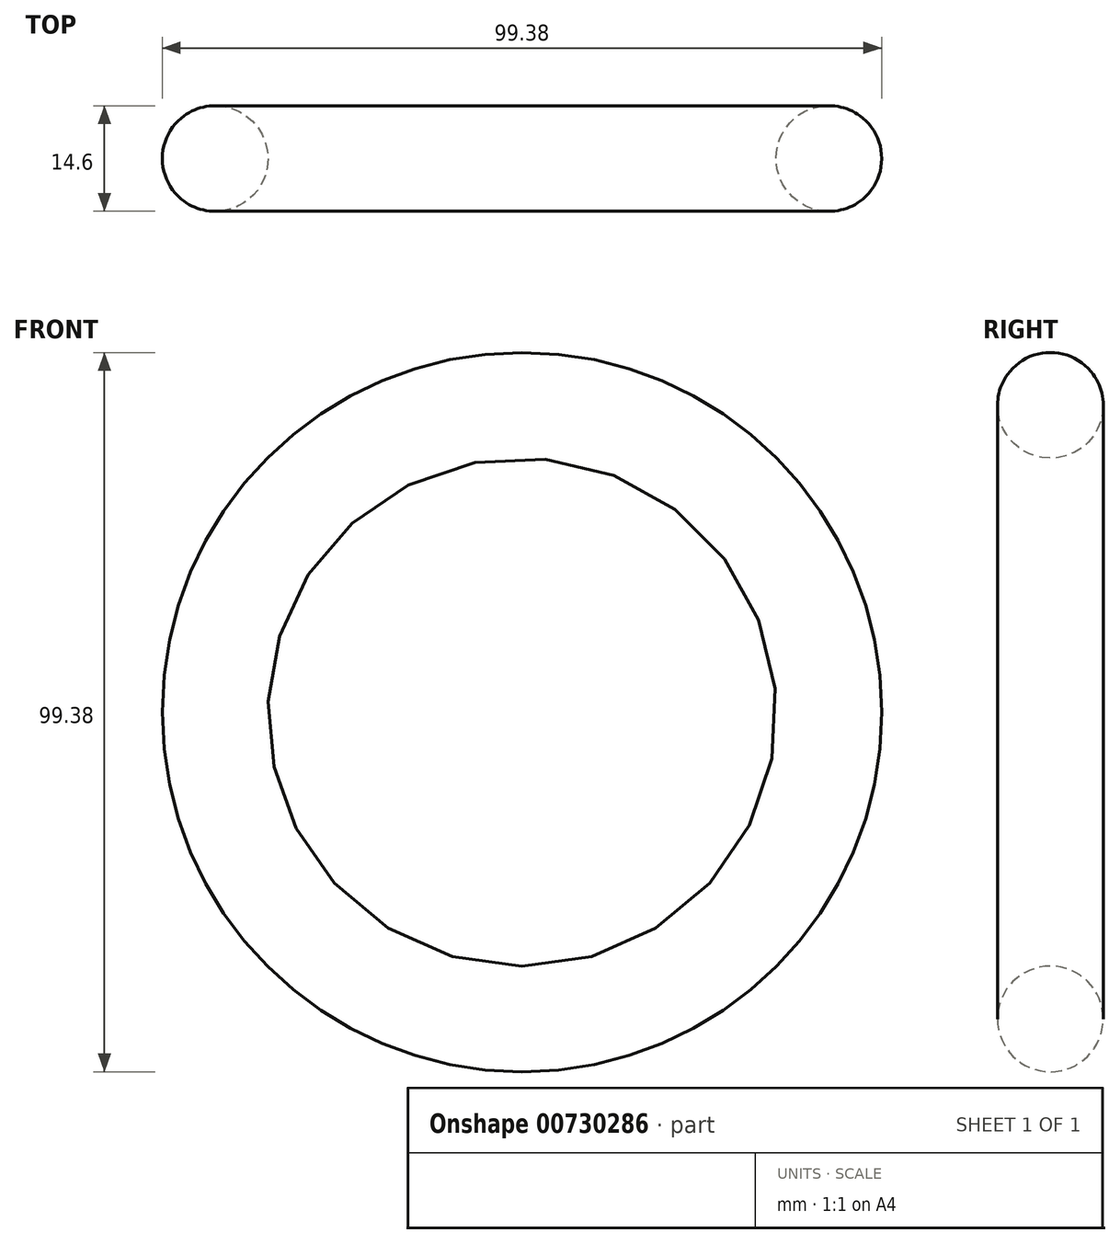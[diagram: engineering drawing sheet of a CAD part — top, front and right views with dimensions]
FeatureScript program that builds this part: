
annotation { "Feature Type Name" : "Feature", "Feature Type Description" : "" }
export const myFeature = defineFeature(function(context is Context, id is Id, definition is map)
    precondition{}
    {
        {
            var Q0;
            Q0=qCreatedBy(makeId("Front.planeOp"),FACE);
            var sketch = newSketch(context, id + "F0", { "sketchPlane" : qUnion([Q0])});
            skCircle(sketch, "E0", {"center": v(0, 0) * mm, "radius": 42.39 * mm});
            skSolve(sketch);
        }
        {
            var Q0;
            Q0=qCreatedBy(makeId("Top.planeOp"),FACE);
            var sketch = newSketch(context, id + "F1", { "sketchPlane" : qUnion([Q0])});
            skCircle(sketch, "E1", {"center": v(42.39, 0) * mm, "radius": 7.3 * mm});
            skLineSegment(sketch, "E2.0", {"start": v(42.39, 0) * mm, "end": v(-42.39, 0) * mm});
            skSolve(sketch);
        }
        {
            var Q0;
            Q0=makeQuery(id+"F1.imprint","IMPRINT",FACE,{"disambiguationData":[TD([[makeQuery(id+"F1.imprint","IMPRINT",EDGE,{"derivedFrom":sQuery(id+"F1.wireOp",EDGE,"E1")}),1.0]])]});
            var Q1;
            Q1=sQuery(id+"F0.wireOp",EDGE,"E0");
            sweep(context, id + "F2", {"profiles" : qUnion([Q0]), "path" : qUnion([Q1])});
        }
    });
